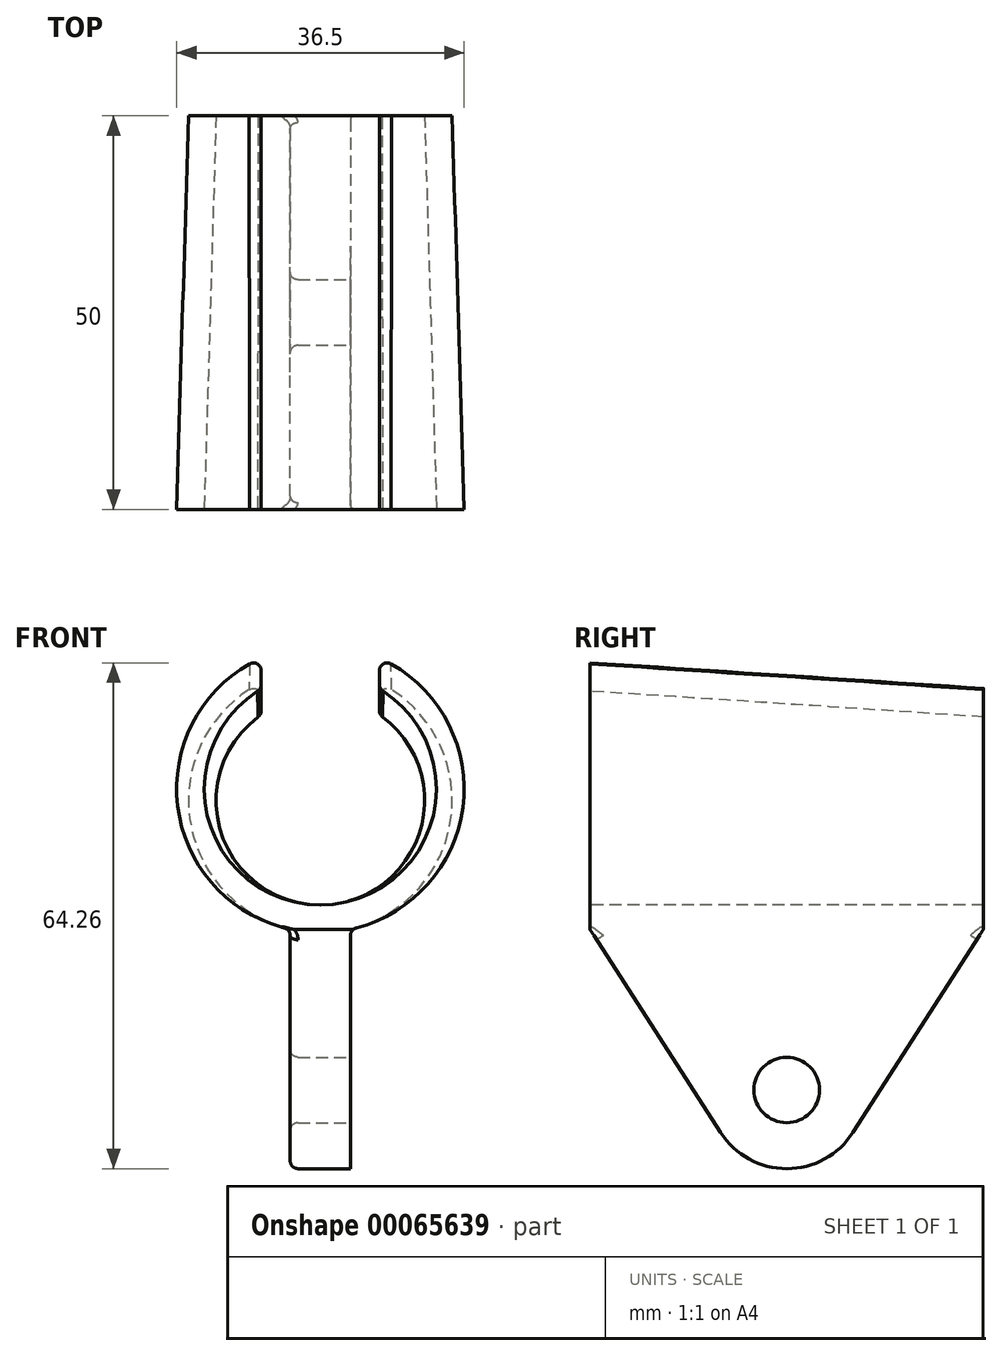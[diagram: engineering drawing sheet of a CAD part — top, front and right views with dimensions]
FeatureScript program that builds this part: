
annotation { "Feature Type Name" : "Feature", "Feature Type Description" : "" }
export const myFeature = defineFeature(function(context is Context, id is Id, definition is map)
    precondition{}
    {
        {
            var Q0;
            Q0=qCreatedBy(makeId("Front.planeOp"),FACE);
            var sketch = newSketch(context, id + "F0", { "sketchPlane" : qUnion([Q0])});
            skCircle(sketch, "E0", {"center": v(0, 18.25) * mm, "radius": 18.25 * mm});
            skSolve(sketch);
        }
        {
            var Q0;
            Q0=qCreatedBy(makeId("Front.planeOp"),FACE);
            cPlane(context, id + "F1", {"entities" : qUnion([Q0]), "cplaneType" : CPlaneType.OFFSET, "offset" : 50 * mm, "oppositeDirection" : true, "width" : 150 * mm, "height" : 150 * mm});
        }
        {
            var Q0;
            Q0=qCreatedBy(id+"F1.planeOp",FACE);
            var sketch = newSketch(context, id + "F2", { "sketchPlane" : qUnion([Q0])});
            skCircle(sketch, "E1", {"center": v(0, 16.75) * mm, "radius": 16.75 * mm});
            skSolve(sketch);
        }
        {
            var Q0;
            Q0=makeQuery(id+"F0.imprint","IMPRINT",FACE,{"disambiguationData":[TD([[makeQuery(id+"F0.imprint","IMPRINT",EDGE,{"derivedFrom":sQuery(id+"F0.wireOp",EDGE,"E0")}),1.0]])]});
            var Q1;
            Q1=makeQuery(id+"F2.imprint","IMPRINT",FACE,{"disambiguationData":[TD([[makeQuery(id+"F2.imprint","IMPRINT",EDGE,{"derivedFrom":sQuery(id+"F2.wireOp",EDGE,"E1")}),1.0]])]});
            loft(context, id + "F3", {"sheetProfilesArray" : [{ "sheetProfileEntities" : qUnion([Q0]) }, { "sheetProfileEntities" : qUnion([Q1]) }]});
        }
        {
            var Q0;
            Q0=makeQuery(id+"F3.opLoft","CAP_FACE",FACE,{"disambiguationData":[OSD([makeQuery(id+"F0.imprint","IMPRINT",FACE,{"disambiguationData":[TD([[makeQuery(id+"F0.imprint","IMPRINT",EDGE,{"derivedFrom":sQuery(id+"F0.wireOp",EDGE,"E0")}),1.0]])]})])],"isStart":true});
            var Q1;
            Q1=makeQuery(id+"F3.opLoft","CAP_FACE",FACE,{"disambiguationData":[OSD([makeQuery(id+"F2.imprint","IMPRINT",FACE,{"disambiguationData":[TD([[makeQuery(id+"F2.imprint","IMPRINT",EDGE,{"derivedFrom":sQuery(id+"F2.wireOp",EDGE,"E1")}),1.0]])]})])],"isStart":true});
            shell(context, id + "F4", {"entities" : qUnion([Q0, Q1]), "thickness" : 3.5 * mm});
        }
        {
            var Q0;
            Q0=qCreatedBy(makeId("Front.planeOp"),FACE);
            var sketch = newSketch(context, id + "F5", { "sketchPlane" : qUnion([Q0])});
            skLineSegment(sketch, "E2.bottom", {"start": v(-7.5, 50.26) * mm, "end": v(7.5, 50.26) * mm});
            skLineSegment(sketch, "E2.top", {"start": v(-7.5, 20) * mm, "end": v(7.5, 20) * mm});
            skLineSegment(sketch, "E2.left", {"start": v(-7.5, 50.26) * mm, "end": v(-7.5, 20) * mm});
            skLineSegment(sketch, "E2.right", {"start": v(7.5, 50.26) * mm, "end": v(7.5, 20) * mm});
            skSolve(sketch);
        }
        {
            var Q0;
            Q0=makeQuery(id+"F5.imprint","IMPRINT",FACE,{"disambiguationData":[TD([[makeQuery(id+"F5.imprint","IMPRINT",EDGE,{"derivedFrom":sQuery(id+"F5.wireOp",EDGE,"E2.bottom")}),-1.0]])]});
            extrude(context, id + "F6", {"entities" : qUnion([Q0]), "operationType" : NewBodyOperationType.REMOVE, "oppositeDirection" : true, "depth" : 67.55 * mm});
        }
        {
            var Q0;
            Q0=qCreatedBy(makeId("Front.planeOp"),FACE);
            cPlane(context, id + "F7", {"entities" : qUnion([Q0]), "cplaneType" : CPlaneType.OFFSET, "offset" : 25 * mm, "oppositeDirection" : true, "width" : 150 * mm, "height" : 150 * mm});
        }
        {
            var Q0;
            Q0=qCreatedBy(id+"F7.planeOp",FACE);
            var sketch = newSketch(context, id + "F8", { "sketchPlane" : qUnion([Q0])});
            skLineSegment(sketch, "E3.left", {"start": v(-3.83, 0.92) * mm, "end": v(-3.83, -30) * mm});
            skPoint(sketch, "E4.orphan", {"position": v(-7.5, 34.89) * mm});
            skPoint(sketch, "E5.orphan", {"position": v(7.5, 34.89) * mm});
            skLineSegment(sketch, "E6", {"start": v(-3.83, -30) * mm, "end": v(0, -30) * mm});
            skLineSegment(sketch, "E7.MirrorCS", {"start": v(3.83, 0.92) * mm, "end": v(3.83, -30) * mm});
            skLineSegment(sketch, "E8.MirrorCS", {"start": v(3.83, -30) * mm, "end": v(0, -30) * mm});
            skLineSegment(sketch, "E9", {"start": v(-3.83, 0.92) * mm, "end": v(3.83, 0.92) * mm});
            skSolve(sketch);
        }
        {
            var Q0;
            Q0=makeQuery(id+"F8.imprint","IMPRINT",FACE,{"disambiguationData":[TD([[makeQuery(id+"F8.imprint","IMPRINT",EDGE,{"derivedFrom":sQuery(id+"F8.wireOp",EDGE,"E3.left")}),1.0]])]});
            var Q1;
            Q1=makeQuery(id+"F3.opLoft","CAP_FACE",FACE,{"disambiguationData":[OSD([makeQuery(id+"F0.imprint","IMPRINT",FACE,{"disambiguationData":[TD([[makeQuery(id+"F0.imprint","IMPRINT",EDGE,{"derivedFrom":sQuery(id+"F0.wireOp",EDGE,"E0")}),1.0]])]})])],"isStart":true});
            var Q2;
            Q2=makeQuery(id+"F3.opLoft","CAP_FACE",FACE,{"disambiguationData":[OSD([makeQuery(id+"F2.imprint","IMPRINT",FACE,{"disambiguationData":[TD([[makeQuery(id+"F2.imprint","IMPRINT",EDGE,{"derivedFrom":sQuery(id+"F2.wireOp",EDGE,"E1")}),1.0]])]})])],"isStart":true});
            extrude(context, id + "F9", {"entities" : qUnion([Q0]), "operationType" : NewBodyOperationType.ADD, "endBound" : BoundingType.UP_TO_SURFACE, "endBoundEntityFace" : qUnion([Q1]), "depth" : 25 * mm, "hasSecondDirection" : true, "secondDirectionBound" : SecondDirectionBoundingType.UP_TO_SURFACE, "secondDirectionOppositeDirection" : true, "secondDirectionBoundEntityFace" : qUnion([Q2]), "secondDirectionDepth" : 25 * mm});
        }
        {
            var Q0;
            Q0=makeQuery(id+"F9.opExtrude","SWEPT_FACE",FACE,{"disambiguationData":[OSD([sQuery(id+"F8.wireOp",EDGE,"E7.MirrorCS")])]});
            var sketch = newSketch(context, id + "F10", { "sketchPlane" : qUnion([Q0])});
            skCircle(sketch, "E10", {"center": v(25, -20) * mm, "radius": 4.16 * mm});
            skArc(sketch, "E11", {"start": v(16.59, -25.4) * mm, "mid": v(25, -30) * mm, "end": v(33.42, -25.4) * mm});
            skLineSegment(sketch, "E12", {"start": v(0, 0.4) * mm, "end": v(16.59, -25.4) * mm});
            skLineSegment(sketch, "E13", {"start": v(50, 0.44) * mm, "end": v(33.42, -25.4) * mm});
            skSolve(sketch);
        }
        {
            var Q0;
            {var subQ0=sQuery(id+"F10.wireOp",EDGE,"E12");Q0=makeQuery(id+"F10.imprint","IMPRINT",FACE,{"disambiguationData":[TD([[makeQuery(id+"F10.imprint","IMPRINT",EDGE,{"derivedFrom":subQ0}),-1.0]])]});}
            var Q1;
            {var subQ0=sQuery(id+"F10.wireOp",EDGE,"E13");Q1=makeQuery(id+"F10.imprint","IMPRINT",FACE,{"disambiguationData":[TD([[makeQuery(id+"F10.imprint","IMPRINT",EDGE,{"derivedFrom":subQ0}),1.0]])]});}
            extrude(context, id + "F11", {"entities" : qUnion([Q0, Q1]), "operationType" : NewBodyOperationType.REMOVE, "endBound" : BoundingType.THROUGH_ALL, "oppositeDirection" : true, "depth" : 25 * mm});
        }
        {
            var Q0;
            Q0=makeQuery(id+"F10.imprint","IMPRINT",FACE,{"disambiguationData":[TD([[makeQuery(id+"F10.imprint","IMPRINT",EDGE,{"derivedFrom":sQuery(id+"F10.wireOp",EDGE,"E10")}),1.0]])]});
            extrude(context, id + "F12", {"entities" : qUnion([Q0]), "operationType" : NewBodyOperationType.REMOVE, "endBound" : BoundingType.THROUGH_ALL, "oppositeDirection" : true, "depth" : 25 * mm});
        }
        {
            var Q0;
            Q0=makeQuery(id+"F6.boolean.opBoolean","INTERSECT",EDGE,{"derivedFrom":[makeQuery(id+"F3.opLoft","SWEPT_FACE",FACE,{"disambiguationData":[OSD([sQuery(id+"F0.wireOp",EDGE,"E0"),sQuery(id+"F2.wireOp",EDGE,"E1")])]}),makeQuery(id+"F6.opExtrude","SWEPT_FACE",FACE,{"disambiguationData":[OSD([sQuery(id+"F5.wireOp",EDGE,"E2.left")])]})]});
            var Q1;
            Q1=makeQuery(id+"F6.boolean.opBoolean","INTERSECT",EDGE,{"derivedFrom":[makeQuery(id+"F4.opShell","OFFSET_FACE",FACE,{"disambiguationData":[OSD([sQuery(id+"F0.wireOp",EDGE,"E0"),sQuery(id+"F2.wireOp",EDGE,"E1")])]}),makeQuery(id+"F6.opExtrude","SWEPT_FACE",FACE,{"disambiguationData":[OSD([sQuery(id+"F5.wireOp",EDGE,"E2.left")])]})]});
            var Q2;
            Q2=makeQuery(id+"F6.boolean.opBoolean","INTERSECT",EDGE,{"derivedFrom":[makeQuery(id+"F3.opLoft","SWEPT_FACE",FACE,{"disambiguationData":[OSD([sQuery(id+"F0.wireOp",EDGE,"E0"),sQuery(id+"F2.wireOp",EDGE,"E1")])]}),makeQuery(id+"F6.opExtrude","SWEPT_FACE",FACE,{"disambiguationData":[OSD([sQuery(id+"F5.wireOp",EDGE,"E2.right")])]})]});
            var Q3;
            Q3=makeQuery(id+"F6.boolean.opBoolean","INTERSECT",EDGE,{"derivedFrom":[makeQuery(id+"F4.opShell","OFFSET_FACE",FACE,{"disambiguationData":[OSD([sQuery(id+"F0.wireOp",EDGE,"E0"),sQuery(id+"F2.wireOp",EDGE,"E1")])]}),makeQuery(id+"F6.opExtrude","SWEPT_FACE",FACE,{"disambiguationData":[OSD([sQuery(id+"F5.wireOp",EDGE,"E2.right")])]})]});
            var Q4;
            Q4=makeQuery(id+"F9.boolean.opBoolean","INTERSECT",EDGE,{"derivedFrom":[makeQuery(id+"F3.opLoft","SWEPT_FACE",FACE,{"disambiguationData":[OSD([sQuery(id+"F0.wireOp",EDGE,"E0"),sQuery(id+"F2.wireOp",EDGE,"E1")])]}),makeQuery(id+"F9.opExtrude","SWEPT_FACE",FACE,{"disambiguationData":[OSD([sQuery(id+"F8.wireOp",EDGE,"E7.MirrorCS")])]})]});
            var Q5;
            Q5=makeQuery(id+"F9.boolean.opBoolean","INTERSECT",EDGE,{"derivedFrom":[makeQuery(id+"F3.opLoft","SWEPT_FACE",FACE,{"disambiguationData":[OSD([sQuery(id+"F0.wireOp",EDGE,"E0"),sQuery(id+"F2.wireOp",EDGE,"E1")])]}),makeQuery(id+"F9.opExtrude","SWEPT_FACE",FACE,{"disambiguationData":[OSD([sQuery(id+"F8.wireOp",EDGE,"E3.left")])]})]});
            fillet(context, id + "F13", {"entities" : qUnion([Q0, Q1, Q2, Q3, Q4, Q5]), "radius" : 1 * mm, "tangentPropagation" : true, "allowEdgeOverflow" : false});
        }
        {
            var Q0;
            Q0=makeQuery(id+"F11.boolean.opBoolean","COPY",EDGE,{"derivedFrom":makeQuery(id+"F11.opExtrude","CAP_EDGE",EDGE,{"disambiguationData":[OSD([sQuery(id+"F10.wireOp",EDGE,"E12")])],"isStart":true})});
            var Q1;
            Q1=makeQuery(id+"F11.boolean.opBoolean","INTERSECT",EDGE,{"derivedFrom":[makeQuery(id+"F9.opExtrude","SWEPT_FACE",FACE,{"disambiguationData":[OSD([sQuery(id+"F8.wireOp",EDGE,"E3.left")])]}),makeQuery(id+"F11.opExtrude","SWEPT_FACE",FACE,{"disambiguationData":[OSD([sQuery(id+"F10.wireOp",EDGE,"E12")])]})]});
            var Q2;
            Q2=makeQuery(id+"F12.boolean.opBoolean","COPY",EDGE,{"derivedFrom":makeQuery(id+"F12.opExtrude","CAP_EDGE",EDGE,{"disambiguationData":[OSD([sQuery(id+"F10.wireOp",EDGE,"E10")])],"isStart":true})});
            var Q3;
            Q3=makeQuery(id+"F12.boolean.opBoolean","INTERSECT",EDGE,{"derivedFrom":[makeQuery(id+"F9.opExtrude","SWEPT_FACE",FACE,{"disambiguationData":[OSD([sQuery(id+"F8.wireOp",EDGE,"E3.left")])]}),makeQuery(id+"F12.opExtrude","SWEPT_FACE",FACE,{"disambiguationData":[OSD([sQuery(id+"F10.wireOp",EDGE,"E10")])]})]});
            fillet(context, id + "F14", {"entities" : qUnion([Q0, Q1, Q2, Q3]), "radius" : 1 * mm, "tangentPropagation" : true, "allowEdgeOverflow" : false});
        }
    });
